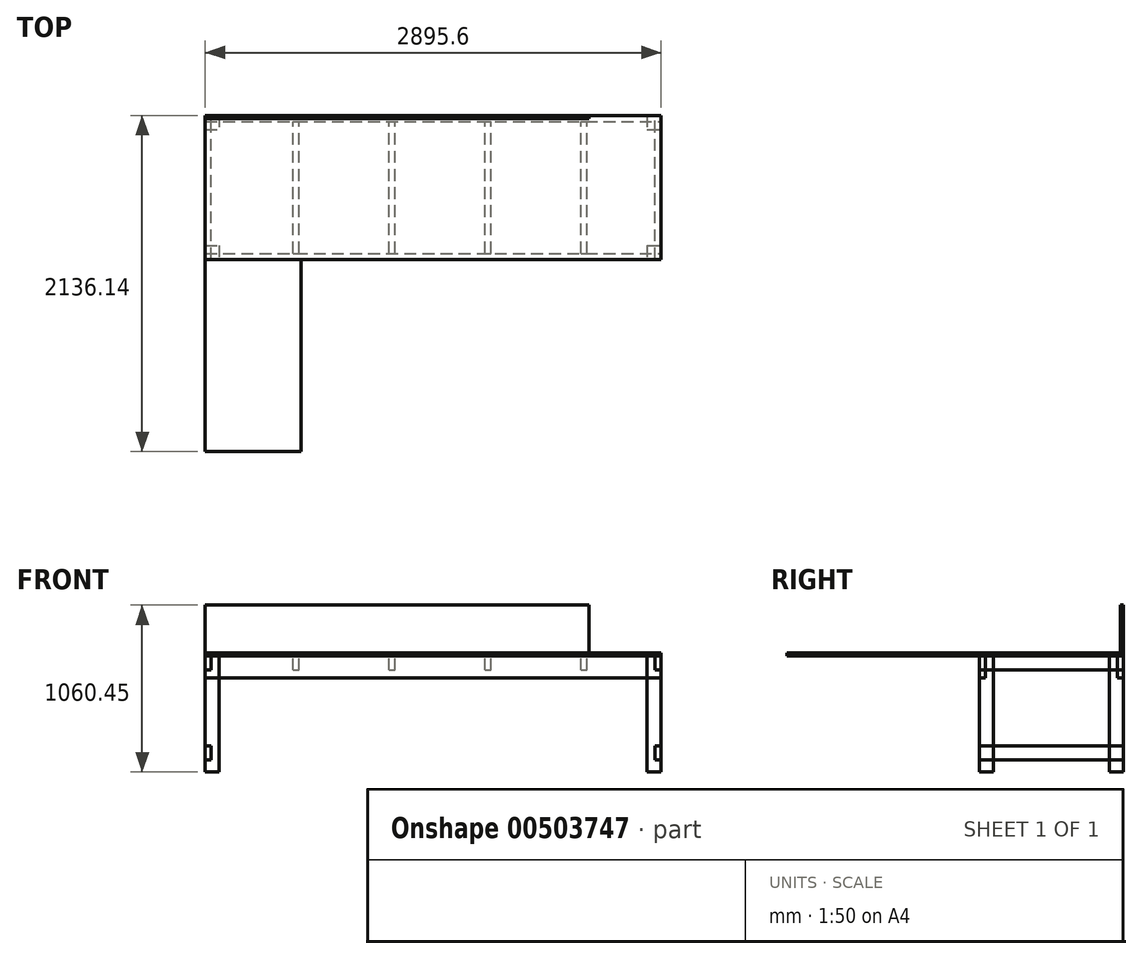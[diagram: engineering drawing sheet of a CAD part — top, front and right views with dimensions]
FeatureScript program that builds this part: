
annotation { "Feature Type Name" : "Feature", "Feature Type Description" : "" }
export const myFeature = defineFeature(function(context is Context, id is Id, definition is map)
    precondition{}
    {
        {
            var Q0;
            Q0=qCreatedBy(makeId("Top.planeOp"),FACE);
            var sketch = newSketch(context, id + "F0", { "sketchPlane" : qUnion([Q0])});
            skLineSegment(sketch, "E0.bottom", {"start": v(0, 0) * mm, "end": v(88.9, 0) * mm});
            skLineSegment(sketch, "E0.top", {"start": v(0, -88.9) * mm, "end": v(88.9, -88.9) * mm});
            skLineSegment(sketch, "E0.left", {"start": v(0, 0) * mm, "end": v(0, -88.9) * mm});
            skLineSegment(sketch, "E0.right", {"start": v(88.9, 0) * mm, "end": v(88.9, -88.9) * mm});
            skLineSegment(sketch, "E1.0.1.0", {"start": v(0, 736.6) * mm, "end": v(88.9, 736.6) * mm});
            skLineSegment(sketch, "E1.0.1.1", {"start": v(0, 825.5) * mm, "end": v(0, 736.6) * mm});
            skLineSegment(sketch, "E1.0.1.2", {"start": v(88.9, 825.5) * mm, "end": v(88.9, 736.6) * mm});
            skLineSegment(sketch, "E1.0.1.3", {"start": v(0, 825.5) * mm, "end": v(88.9, 825.5) * mm});
            skLineSegment(sketch, "E1.1.0.0", {"start": v(2806.7, -88.9) * mm, "end": v(2895.6, -88.9) * mm});
            skLineSegment(sketch, "E1.1.0.1", {"start": v(2806.7, 0) * mm, "end": v(2806.7, -88.9) * mm});
            skLineSegment(sketch, "E1.1.0.2", {"start": v(2895.6, 0) * mm, "end": v(2895.6, -88.9) * mm});
            skLineSegment(sketch, "E1.1.0.3", {"start": v(2806.7, 0) * mm, "end": v(2895.6, 0) * mm});
            skLineSegment(sketch, "E1.1.1.0", {"start": v(2806.7, 736.6) * mm, "end": v(2895.6, 736.6) * mm});
            skLineSegment(sketch, "E1.1.1.1", {"start": v(2806.7, 825.5) * mm, "end": v(2806.7, 736.6) * mm});
            skLineSegment(sketch, "E1.1.1.2", {"start": v(2895.6, 825.5) * mm, "end": v(2895.6, 736.6) * mm});
            skLineSegment(sketch, "E1.1.1.3", {"start": v(2806.7, 825.5) * mm, "end": v(2895.6, 825.5) * mm});
            skLineSegment(sketch, "E1.direction1", {"start": v(0, -88.9) * mm, "end": v(2806.7, -88.9) * mm, "construction": true});
            skLineSegment(sketch, "E1.direction2", {"start": v(0, -88.9) * mm, "end": v(0, 736.6) * mm, "construction": true});
            skSolve(sketch);
        }
        {
            var Q0;
            Q0 = qSketchRegion(id + "F0", true);
            extrude(context, id + "F1", {"entities" : qUnion([Q0]), "depth" : 736.6 * mm});
        }
        {
            var Q0;
            Q0=makeQuery(id+"F1.opExtrude","CAP_FACE",FACE,{"disambiguationData":[OSD([sQuery(id+"F0.wireOp",EDGE,"E0.bottom"),sQuery(id+"F0.wireOp",EDGE,"E0.top"),sQuery(id+"F0.wireOp",EDGE,"E0.left"),sQuery(id+"F0.wireOp",EDGE,"E0.right")])],"isStart":false});
            var sketch = newSketch(context, id + "F2", { "sketchPlane" : qUnion([Q0])});
            skLineSegment(sketch, "E2.bottom", {"start": v(0, -88.9) * mm, "end": v(2895.6, -88.9) * mm});
            skLineSegment(sketch, "E2.top", {"start": v(0, 825.5) * mm, "end": v(2895.6, 825.5) * mm});
            skLineSegment(sketch, "E2.left", {"start": v(0, -88.9) * mm, "end": v(0, 825.5) * mm});
            skLineSegment(sketch, "E2.right", {"start": v(2895.6, -88.9) * mm, "end": v(2895.6, 825.5) * mm});
            skLineSegment(sketch, "E3.bottom", {"start": v(0, -91.44) * mm, "end": v(609.6, -91.44) * mm});
            skLineSegment(sketch, "E3.top", {"start": v(0, -1310.64) * mm, "end": v(609.6, -1310.64) * mm});
            skLineSegment(sketch, "E3.left", {"start": v(0, -91.44) * mm, "end": v(0, -1310.64) * mm});
            skLineSegment(sketch, "E3.right", {"start": v(609.6, -91.44) * mm, "end": v(609.6, -1310.64) * mm});
            skLineSegment(sketch, "E4", {"start": v(457.2, 825.5) * mm, "end": v(457.2, -88.9) * mm, "construction": true});
            skLineSegment(sketch, "E5.bottom", {"start": v(0, 825.5) * mm, "end": v(2895.6, 825.5) * mm, "construction": true});
            skLineSegment(sketch, "E5.top", {"start": v(0, -2070.1) * mm, "end": v(2895.6, -2070.1) * mm, "construction": true});
            skLineSegment(sketch, "E5.left", {"start": v(0, 825.5) * mm, "end": v(0, -2070.1) * mm, "construction": true});
            skLineSegment(sketch, "E5.right", {"start": v(2895.6, 825.5) * mm, "end": v(2895.6, -2070.1) * mm, "construction": true});
            skSolve(sketch);
        }
        {
            var Q0;
            {var subQ4=makeQuery(id+"F1.opExtrude","CAP_EDGE",EDGE,{"disambiguationData":[OSD([sQuery(id+"F0.wireOp",EDGE,"E0.bottom")])],"isStart":false});Q0=makeQuery(id+"F2.imprint","IMPRINT",FACE,{"disambiguationData":[TD([[makeQuery(id+"F2.imprint","IMPRINT",EDGE,{"derivedFrom":subQ4}),-1.0]])]});}
            var Q1;
            {var subQ2=sQuery(id+"F2.wireOp",EDGE,"E2.top");Q1=makeQuery(id+"F2.imprint","IMPRINT",FACE,{"disambiguationData":[TD([[makeQuery(id+"F2.imprint","IMPRINT",EDGE,{"derivedFrom":subQ2}),-1.0]])]});}
            var Q2;
            Q2=makeQuery(id+"F2.imprint","IMPRINT",FACE,{"disambiguationData":[TD([[makeQuery(id+"F2.imprint","IMPRINT",EDGE,{"derivedFrom":sQuery(id+"F2.wireOp",EDGE,"E3.bottom")}),-1.0]])]});
            extrude(context, id + "F3", {"entities" : qUnion([Q0, Q1, Q2]), "depth" : 19.05 * mm});
        }
        {
            var Q0;
            Q0=makeQuery(id+"F1.opExtrude","SWEPT_FACE",FACE,{"disambiguationData":[OSD([sQuery(id+"F0.wireOp",EDGE,"E1.1.1.3")])]});
            var sketch = newSketch(context, id + "F4", { "sketchPlane" : qUnion([Q0])});
            skLineSegment(sketch, "E6.bottom", {"start": v(-2895.6, 736.6) * mm, "end": v(-2857.5, 736.6) * mm});
            skLineSegment(sketch, "E6.top", {"start": v(-2895.6, 647.7) * mm, "end": v(-2857.5, 647.7) * mm});
            skLineSegment(sketch, "E6.left", {"start": v(-2895.6, 736.6) * mm, "end": v(-2895.6, 647.7) * mm});
            skLineSegment(sketch, "E6.right", {"start": v(-2857.5, 736.6) * mm, "end": v(-2857.5, 647.7) * mm});
            skLineSegment(sketch, "E7", {"start": v(-1447.8, 755.65) * mm, "end": v(-1447.8, 590.8) * mm, "construction": true});
            skLineSegment(sketch, "E8", {"start": v(-2895.6, 406.4) * mm, "end": v(-3159.42, 406.4) * mm, "construction": true});
            skLineSegment(sketch, "E9.MirrorCS", {"start": v(-2895.6, 165.1) * mm, "end": v(-2857.5, 165.1) * mm});
            skLineSegment(sketch, "E10.MirrorCS", {"start": v(-2895.6, 76.2) * mm, "end": v(-2857.5, 76.2) * mm});
            skLineSegment(sketch, "E11.MirrorCS", {"start": v(-2857.5, 76.2) * mm, "end": v(-2857.5, 165.1) * mm});
            skLineSegment(sketch, "E12.MirrorCS", {"start": v(-2895.6, 76.2) * mm, "end": v(-2895.6, 165.1) * mm});
            skLineSegment(sketch, "E13.MirrorCS", {"start": v(0, 647.7) * mm, "end": v(-38.1, 647.7) * mm});
            skLineSegment(sketch, "E14.MirrorCS", {"start": v(0, 76.2) * mm, "end": v(-38.1, 76.2) * mm});
            skLineSegment(sketch, "E15.MirrorCS", {"start": v(0, 165.1) * mm, "end": v(-38.1, 165.1) * mm});
            skLineSegment(sketch, "E16.MirrorCS", {"start": v(0, 736.6) * mm, "end": v(-38.1, 736.6) * mm});
            skLineSegment(sketch, "E17.MirrorCS", {"start": v(0, 736.6) * mm, "end": v(0, 647.7) * mm});
            skLineSegment(sketch, "E18.MirrorCS", {"start": v(-38.1, 736.6) * mm, "end": v(-38.1, 647.7) * mm});
            skLineSegment(sketch, "E19.MirrorCS", {"start": v(0, 76.2) * mm, "end": v(0, 165.1) * mm});
            skLineSegment(sketch, "E20.MirrorCS", {"start": v(-38.1, 76.2) * mm, "end": v(-38.1, 165.1) * mm});
            skLineSegment(sketch, "E21.MirrorCS", {"start": v(0, 406.4) * mm, "end": v(263.82, 406.4) * mm, "construction": true});
            skSolve(sketch);
        }
        {
            var Q0;
            Q0 = qSketchRegion(id + "F4", true);
            var Q1;
            Q1=makeQuery(id+"F1.opExtrude","SWEPT_FACE",FACE,{"disambiguationData":[OSD([sQuery(id+"F0.wireOp",EDGE,"E1.1.0.0")])]});
            extrude(context, id + "F5", {"entities" : qUnion([Q0]), "endBound" : BoundingType.UP_TO_SURFACE, "oppositeDirection" : true, "endBoundEntityFace" : qUnion([Q1]), "depth" : 25.4 * mm});
        }
        {
            var Q0;
            Q0=makeQuery(id+"F1.opExtrude","SWEPT_FACE",FACE,{"disambiguationData":[OSD([sQuery(id+"F0.wireOp",EDGE,"E1.1.1.2")])]});
            var sketch = newSketch(context, id + "F6", { "sketchPlane" : qUnion([Q0])});
            skLineSegment(sketch, "E22.bottom", {"start": v(-88.9, 736.6) * mm, "end": v(-50.8, 736.6) * mm});
            skLineSegment(sketch, "E22.top", {"start": v(-88.9, 596.9) * mm, "end": v(-50.8, 596.9) * mm});
            skLineSegment(sketch, "E22.left", {"start": v(-88.9, 736.6) * mm, "end": v(-88.9, 596.9) * mm});
            skLineSegment(sketch, "E22.right", {"start": v(-50.8, 736.6) * mm, "end": v(-50.8, 596.9) * mm});
            skLineSegment(sketch, "E23", {"start": v(368.3, 755.65) * mm, "end": v(368.3, 963.6) * mm});
            skLineSegment(sketch, "E24.MirrorCS", {"start": v(825.5, 736.6) * mm, "end": v(787.4, 736.6) * mm});
            skLineSegment(sketch, "E25.MirrorCS", {"start": v(825.5, 596.9) * mm, "end": v(787.4, 596.9) * mm});
            skLineSegment(sketch, "E26.MirrorCS", {"start": v(825.5, 736.6) * mm, "end": v(825.5, 596.9) * mm});
            skLineSegment(sketch, "E27.MirrorCS", {"start": v(787.4, 736.6) * mm, "end": v(787.4, 596.9) * mm});
            skSolve(sketch);
        }
        {
            var Q0;
            Q0 = qSketchRegion(id + "F6", true);
            var Q1;
            Q1=makeQuery(id+"F1.opExtrude","SWEPT_FACE",FACE,{"disambiguationData":[OSD([sQuery(id+"F0.wireOp",EDGE,"E0.left")])]});
            extrude(context, id + "F7", {"entities" : qUnion([Q0]), "endBound" : BoundingType.UP_TO_SURFACE, "oppositeDirection" : true, "endBoundEntityFace" : qUnion([Q1]), "depth" : 25.4 * mm});
        }
        {
            var Q0;
            Q0=makeQuery(id+"F3.opExtrude","CAP_FACE",FACE,{"disambiguationData":[OSD([sQuery(id+"F2.wireOp",EDGE,"E2.bottom"),sQuery(id+"F2.wireOp",EDGE,"E2.top"),sQuery(id+"F2.wireOp",EDGE,"E2.left"),sQuery(id+"F2.wireOp",EDGE,"E2.right")])],"isStart":true});
            var sketch = newSketch(context, id + "F8", { "sketchPlane" : qUnion([Q0])});
            skLineSegment(sketch, "E28.bottom", {"start": v(558.8, 50.8) * mm, "end": v(596.9, 50.8) * mm});
            skLineSegment(sketch, "E28.top", {"start": v(558.8, -787.4) * mm, "end": v(596.9, -787.4) * mm});
            skLineSegment(sketch, "E28.left", {"start": v(558.8, 50.8) * mm, "end": v(558.8, -787.4) * mm});
            skLineSegment(sketch, "E28.right", {"start": v(596.9, 50.8) * mm, "end": v(596.9, -787.4) * mm});
            skLineSegment(sketch, "E29.1.0.0", {"start": v(1206.5, 50.8) * mm, "end": v(1206.5, -787.4) * mm});
            skLineSegment(sketch, "E29.1.0.1", {"start": v(1168.4, 50.8) * mm, "end": v(1168.4, -787.4) * mm});
            skLineSegment(sketch, "E29.1.0.2", {"start": v(1168.4, -787.4) * mm, "end": v(1206.5, -787.4) * mm});
            skLineSegment(sketch, "E29.1.0.3", {"start": v(1168.4, 50.8) * mm, "end": v(1206.5, 50.8) * mm});
            skLineSegment(sketch, "E29.2.0.0", {"start": v(1816.1, 50.8) * mm, "end": v(1816.1, -787.4) * mm});
            skLineSegment(sketch, "E29.2.0.1", {"start": v(1778, 50.8) * mm, "end": v(1778, -787.4) * mm});
            skLineSegment(sketch, "E29.2.0.2", {"start": v(1778, -787.4) * mm, "end": v(1816.1, -787.4) * mm});
            skLineSegment(sketch, "E29.2.0.3", {"start": v(1778, 50.8) * mm, "end": v(1816.1, 50.8) * mm});
            skLineSegment(sketch, "E29.3.0.0", {"start": v(2425.7, 50.8) * mm, "end": v(2425.7, -787.4) * mm});
            skLineSegment(sketch, "E29.3.0.1", {"start": v(2387.6, 50.8) * mm, "end": v(2387.6, -787.4) * mm});
            skLineSegment(sketch, "E29.3.0.2", {"start": v(2387.6, -787.4) * mm, "end": v(2425.7, -787.4) * mm});
            skLineSegment(sketch, "E29.3.0.3", {"start": v(2387.6, 50.8) * mm, "end": v(2425.7, 50.8) * mm});
            skLineSegment(sketch, "E29.direction1", {"start": v(558.8, -787.4) * mm, "end": v(1168.4, -787.4) * mm, "construction": true});
            skSolve(sketch);
        }
        {
            var Q0;
            Q0 = qSketchRegion(id + "F8", true);
            extrude(context, id + "F9", {"entities" : qUnion([Q0]), "depth" : 88.9 * mm});
        }
        {
            var Q0;
            Q0=makeQuery(id+"F3.opExtrude","CAP_FACE",FACE,{"disambiguationData":[OSD([sQuery(id+"F2.wireOp",EDGE,"E2.bottom"),sQuery(id+"F2.wireOp",EDGE,"E2.top"),sQuery(id+"F2.wireOp",EDGE,"E2.left"),sQuery(id+"F2.wireOp",EDGE,"E2.right")])],"isStart":false});
            var sketch = newSketch(context, id + "F10", { "sketchPlane" : qUnion([Q0])});
            skLineSegment(sketch, "E30.bottom", {"start": v(0, 825.5) * mm, "end": v(2438.4, 825.5) * mm});
            skLineSegment(sketch, "E30.top", {"start": v(0, 806.45) * mm, "end": v(2438.4, 806.45) * mm});
            skLineSegment(sketch, "E30.left", {"start": v(0, 825.5) * mm, "end": v(0, 806.45) * mm});
            skLineSegment(sketch, "E30.right", {"start": v(2438.4, 825.5) * mm, "end": v(2438.4, 806.45) * mm});
            skSolve(sketch);
        }
        {
            var Q0;
            Q0 = qSketchRegion(id + "F10", true);
            extrude(context, id + "F11", {"entities" : qUnion([Q0]), "operationType" : NewBodyOperationType.ADD, "depth" : 304.8 * mm});
        }
    });
